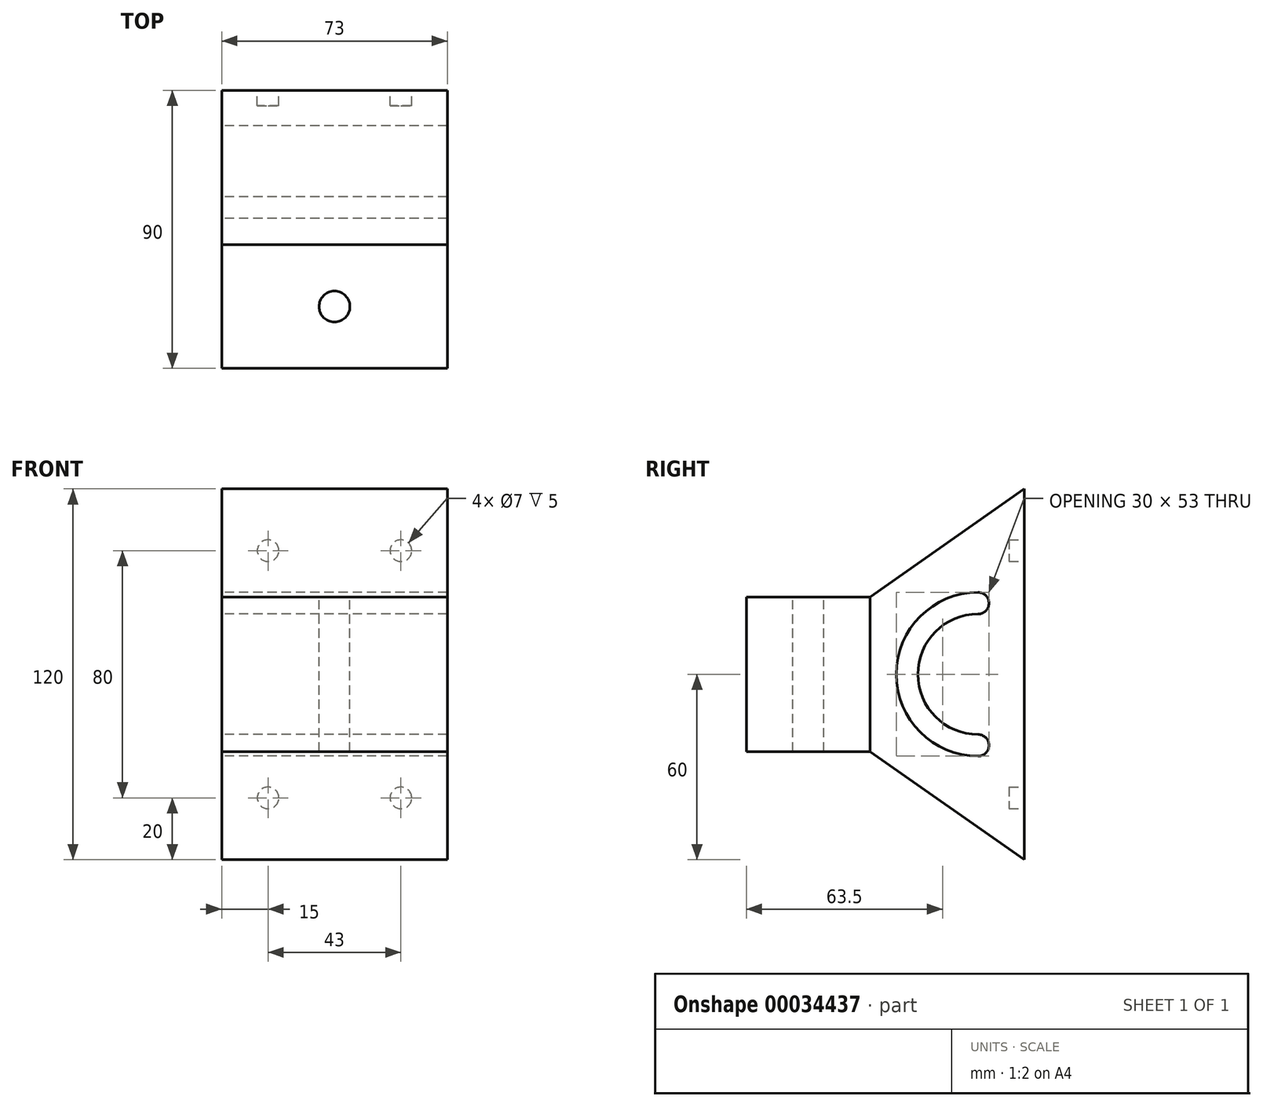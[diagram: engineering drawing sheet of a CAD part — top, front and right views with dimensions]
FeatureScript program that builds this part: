
annotation { "Feature Type Name" : "Feature", "Feature Type Description" : "" }
export const myFeature = defineFeature(function(context is Context, id is Id, definition is map)
    precondition{}
    {
        {
            var Q0;
            Q0=qCreatedBy(makeId("Front.planeOp"),FACE);
            var sketch = newSketch(context, id + "F0", { "sketchPlane" : qUnion([Q0])});
            skLineSegment(sketch, "E0.rect.bottom", {"start": v(36.5, -60) * mm, "end": v(-36.5, -60) * mm});
            skLineSegment(sketch, "E0.rect.top", {"start": v(36.5, 60) * mm, "end": v(-36.5, 60) * mm});
            skLineSegment(sketch, "E0.rect.left", {"start": v(36.5, -60) * mm, "end": v(36.5, 60) * mm});
            skLineSegment(sketch, "E0.rect.right", {"start": v(-36.5, -60) * mm, "end": v(-36.5, 60) * mm});
            skPoint(sketch, "E0.rect.middle", {"position": v(0, 0) * mm});
            skSolve(sketch);
        }
        {
            var Q0;
            Q0 = qSketchRegion(id + "F0", true);
            extrude(context, id + "F1", {"entities" : qUnion([Q0]), "depth" : 50 * mm});
        }
        {
            var Q0;
            Q0=makeQuery(id+"F1.opExtrude","SWEPT_FACE",FACE,{"disambiguationData":[OSD([sQuery(id+"F0.wireOp",EDGE,"E0.rect.right")])]});
            var sketch = newSketch(context, id + "F2", { "sketchPlane" : qUnion([Q0])});
            skPoint(sketch, "E1", {"position": v(15, 19.5) * mm});
            skPoint(sketch, "E2", {"position": v(15, -19.5) * mm});
            skPoint(sketch, "E3", {"position": v(15, 26.5) * mm});
            skPoint(sketch, "E4", {"position": v(15, -26.5) * mm});
            skArc(sketch, "E5", {"start": v(15, -19.5) * mm, "mid": v(34.5, 0) * mm, "end": v(15, 19.5) * mm});
            skArc(sketch, "E6", {"start": v(15, -26.5) * mm, "mid": v(41.5, 0) * mm, "end": v(15, 26.5) * mm});
            skArc(sketch, "E7", {"start": v(15, -19.5) * mm, "mid": v(11.5, -23) * mm, "end": v(15, -26.5) * mm});
            skArc(sketch, "E8", {"start": v(15, 26.5) * mm, "mid": v(11.5, 23) * mm, "end": v(15, 19.5) * mm});
            skSolve(sketch);
        }
        {
            var Q0;
            Q0 = qSketchRegion(id + "F2", true);
            extrude(context, id + "F3", {"entities" : qUnion([Q0]), "operationType" : NewBodyOperationType.REMOVE, "oppositeDirection" : true, "depth" : 80 * mm});
        }
        {
            var Q0;
            Q0=makeQuery(id+"F1.opExtrude","SWEPT_FACE",FACE,{"disambiguationData":[OSD([sQuery(id+"F0.wireOp",EDGE,"E0.rect.right")])]});
            var sketch = newSketch(context, id + "F4", { "sketchPlane" : qUnion([Q0])});
            skLineSegment(sketch, "E9", {"start": v(0, 60) * mm, "end": v(50, 25) * mm});
            skLineSegment(sketch, "E10", {"start": v(0, -60) * mm, "end": v(50, -25) * mm});
            skLineSegment(sketch, "E11", {"start": v(0, 60) * mm, "end": v(50, 60) * mm});
            skLineSegment(sketch, "E12", {"start": v(50, 60) * mm, "end": v(50, 25) * mm});
            skLineSegment(sketch, "E13", {"start": v(50, -25) * mm, "end": v(50, -60) * mm});
            skLineSegment(sketch, "E14", {"start": v(50, -60) * mm, "end": v(0, -60) * mm});
            skSolve(sketch);
        }
        {
            var Q0;
            Q0 = qSketchRegion(id + "F4", true);
            extrude(context, id + "F5", {"entities" : qUnion([Q0]), "operationType" : NewBodyOperationType.REMOVE, "oppositeDirection" : true, "depth" : 80 * mm});
        }
        {
            var Q0;
            Q0=makeQuery(id+"F1.opExtrude","CAP_FACE",FACE,{"disambiguationData":[OSD([sQuery(id+"F0.wireOp",EDGE,"E0.rect.bottom"),sQuery(id+"F0.wireOp",EDGE,"E0.rect.top"),sQuery(id+"F0.wireOp",EDGE,"E0.rect.left"),sQuery(id+"F0.wireOp",EDGE,"E0.rect.right")])],"isStart":true});
            var sketch = newSketch(context, id + "F6", { "sketchPlane" : qUnion([Q0])});
            skLineSegment(sketch, "E15", {"start": v(-36.5, 40) * mm, "end": v(36.5, 40) * mm, "construction": true});
            skLineSegment(sketch, "E16", {"start": v(-36.5, -40) * mm, "end": v(36.5, -40) * mm, "construction": true});
            skLineSegment(sketch, "E17", {"start": v(-21.5, 60) * mm, "end": v(-21.5, -60) * mm, "construction": true});
            skLineSegment(sketch, "E18", {"start": v(21.5, 60) * mm, "end": v(21.5, -60) * mm, "construction": true});
            skCircle(sketch, "E19", {"center": v(-21.5, 40) * mm, "radius": 3.5 * mm});
            skCircle(sketch, "E20", {"center": v(21.5, 40) * mm, "radius": 3.5 * mm});
            skCircle(sketch, "E21", {"center": v(-21.5, -40) * mm, "radius": 3.5 * mm});
            skCircle(sketch, "E22", {"center": v(21.5, -40) * mm, "radius": 3.5 * mm});
            skSolve(sketch);
        }
        {
            var Q0;
            Q0 = qSketchRegion(id + "F6", true);
            extrude(context, id + "F7", {"entities" : qUnion([Q0]), "operationType" : NewBodyOperationType.REMOVE, "oppositeDirection" : true, "depth" : 5 * mm});
        }
        {
            var Q0;
            Q0=makeQuery(id+"F1.opExtrude","SWEPT_FACE",FACE,{"disambiguationData":[OSD([sQuery(id+"F0.wireOp",EDGE,"E0.rect.right")])]});
            var sketch = newSketch(context, id + "F8", { "sketchPlane" : qUnion([Q0])});
            skLineSegment(sketch, "E23.bottom", {"start": v(50, 25) * mm, "end": v(90, 25) * mm});
            skLineSegment(sketch, "E23.top", {"start": v(50, -25) * mm, "end": v(90, -25) * mm});
            skLineSegment(sketch, "E23.left", {"start": v(50, 25) * mm, "end": v(50, -25) * mm});
            skLineSegment(sketch, "E23.right", {"start": v(90, 25) * mm, "end": v(90, -25) * mm});
            skSolve(sketch);
        }
        {
            var Q0;
            Q0 = qSketchRegion(id + "F8", true);
            extrude(context, id + "F9", {"entities" : qUnion([Q0]), "oppositeDirection" : true, "depth" : 73 * mm});
        }
        {
            var Q0;
            Q0=makeQuery(id+"F9.opExtrude","SWEPT_FACE",FACE,{"disambiguationData":[OSD([sQuery(id+"F8.wireOp",EDGE,"E23.bottom")])]});
            var sketch = newSketch(context, id + "F10", { "sketchPlane" : qUnion([Q0])});
            skLineSegment(sketch, "E24", {"start": v(-36.5, -70) * mm, "end": v(36.5, -70) * mm, "construction": true});
            skLineSegment(sketch, "E25", {"start": v(0, -50) * mm, "end": v(0, -90) * mm, "construction": true});
            skCircle(sketch, "E26", {"center": v(0, -70) * mm, "radius": 5 * mm});
            skSolve(sketch);
        }
        {
            var Q0;
            Q0 = qSketchRegion(id + "F10", true);
            extrude(context, id + "F11", {"entities" : qUnion([Q0]), "operationType" : NewBodyOperationType.REMOVE, "oppositeDirection" : true, "depth" : 80 * mm});
        }
    });
